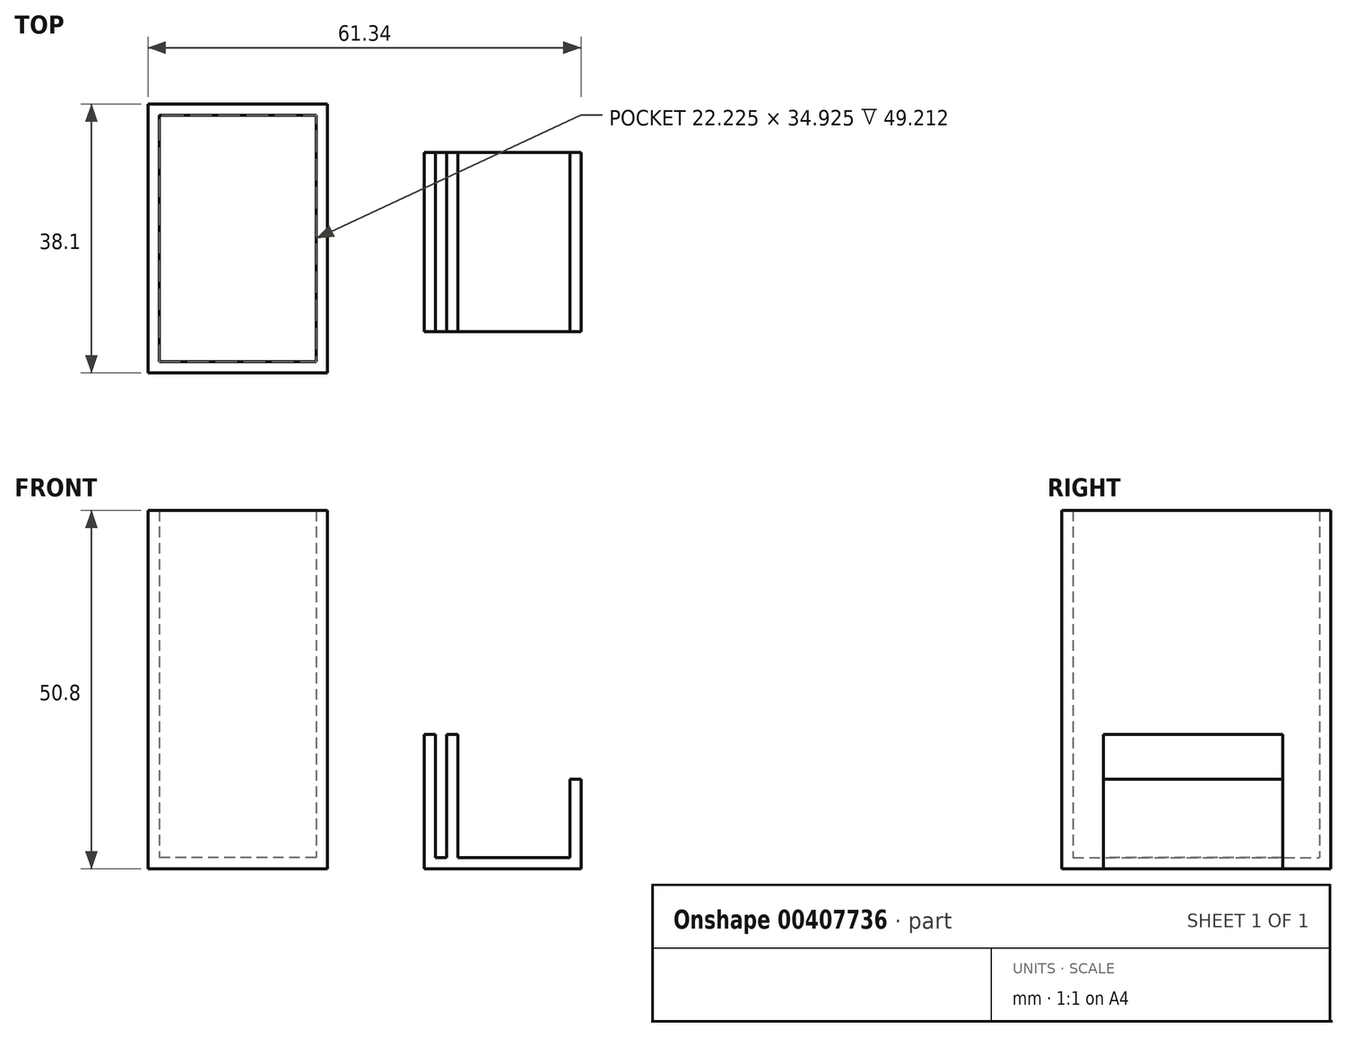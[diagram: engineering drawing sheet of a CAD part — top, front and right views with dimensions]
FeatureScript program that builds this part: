
annotation { "Feature Type Name" : "Feature", "Feature Type Description" : "" }
export const myFeature = defineFeature(function(context is Context, id is Id, definition is map)
    precondition{}
    {
        {
            var Q0;
            Q0=qCreatedBy(makeId("Top.planeOp"),FACE);
            var sketch = newSketch(context, id + "F0", { "sketchPlane" : qUnion([Q0])});
            skLineSegment(sketch, "E0.bottom", {"start": v(0, 0) * mm, "end": v(-25.4, 0) * mm});
            skLineSegment(sketch, "E0.top", {"start": v(0, 38.1) * mm, "end": v(-25.4, 38.1) * mm});
            skLineSegment(sketch, "E0.left", {"start": v(0, 0) * mm, "end": v(0, 38.1) * mm});
            skLineSegment(sketch, "E0.right", {"start": v(-25.4, 0) * mm, "end": v(-25.4, 38.1) * mm});
            skSolve(sketch);
        }
        {
            var Q0;
            Q0=makeQuery(id+"F0.imprint","IMPRINT",FACE,{"disambiguationData":[TD([[makeQuery(id+"F0.imprint","IMPRINT",EDGE,{"derivedFrom":sQuery(id+"F0.wireOp",EDGE,"E0.bottom")}),-1.0]])]});
            extrude(context, id + "F1", {"entities" : qUnion([Q0]), "depth" : 50.8 * mm});
        }
        {
            var Q0;
            Q0=makeQuery(id+"F1.opExtrude","CAP_FACE",FACE,{"disambiguationData":[OSD([sQuery(id+"F0.wireOp",EDGE,"E0.bottom"),sQuery(id+"F0.wireOp",EDGE,"E0.top"),sQuery(id+"F0.wireOp",EDGE,"E0.left"),sQuery(id+"F0.wireOp",EDGE,"E0.right")])],"isStart":false});
            shell(context, id + "F2", {"entities" : qUnion([Q0]), "thickness" : 1.59 * mm});
        }
        {
            var Q0;
            Q0=qCreatedBy(makeId("Top.planeOp"),FACE);
            var sketch = newSketch(context, id + "F3", { "sketchPlane" : qUnion([Q0])});
            skLineSegment(sketch, "E1.bottom", {"start": v(13.71, 5.85) * mm, "end": v(35.94, 5.85) * mm});
            skLineSegment(sketch, "E1.top", {"start": v(13.71, 31.25) * mm, "end": v(35.94, 31.25) * mm});
            skLineSegment(sketch, "E1.left", {"start": v(18.47, 5.85) * mm, "end": v(18.47, 31.25) * mm});
            skLineSegment(sketch, "E1.right", {"start": v(34.35, 5.85) * mm, "end": v(34.35, 31.25) * mm});
            skLineSegment(sketch, "E2.0", {"start": v(35.94, 5.85) * mm, "end": v(35.94, 31.25) * mm});
            skLineSegment(sketch, "E3.0", {"start": v(16.89, 5.85) * mm, "end": v(16.89, 31.25) * mm});
            skLineSegment(sketch, "E4.0", {"start": v(15.3, 5.85) * mm, "end": v(15.3, 31.25) * mm});
            skLineSegment(sketch, "E5.0", {"start": v(13.71, 5.85) * mm, "end": v(13.71, 31.25) * mm});
            skSolve(sketch);
        }
        {
            var Q0;
            {var subQ0=sQuery(id+"F3.wireOp",EDGE,"E1.left");Q0=makeQuery(id+"F3.imprint","IMPRINT",FACE,{"disambiguationData":[TD([[makeQuery(id+"F3.imprint","IMPRINT",EDGE,{"derivedFrom":subQ0}),-1.0]])]});}
            var Q1;
            {var subQ2=sQuery(id+"F3.wireOp",EDGE,"E1.right");Q1=makeQuery(id+"F3.imprint","IMPRINT",FACE,{"disambiguationData":[TD([[makeQuery(id+"F3.imprint","IMPRINT",EDGE,{"derivedFrom":subQ2}),-1.0]])]});}
            var Q2;
            {var subQ0=sQuery(id+"F3.wireOp",EDGE,"E1.left");Q2=makeQuery(id+"F3.imprint","IMPRINT",FACE,{"disambiguationData":[TD([[makeQuery(id+"F3.imprint","IMPRINT",EDGE,{"derivedFrom":subQ0}),1.0]])]});}
            var Q3;
            {var subQ0=sQuery(id+"F3.wireOp",EDGE,"E3.0");Q3=makeQuery(id+"F3.imprint","IMPRINT",FACE,{"disambiguationData":[TD([[makeQuery(id+"F3.imprint","IMPRINT",EDGE,{"derivedFrom":subQ0}),1.0]])]});}
            var Q4;
            {var subQ2=sQuery(id+"F3.wireOp",EDGE,"E4.0");Q4=makeQuery(id+"F3.imprint","IMPRINT",FACE,{"disambiguationData":[TD([[makeQuery(id+"F3.imprint","IMPRINT",EDGE,{"derivedFrom":subQ2}),1.0]])]});}
            extrude(context, id + "F4", {"entities" : qUnion([Q0, Q1, Q2, Q3, Q4]), "depth" : 1.59 * mm});
        }
        {
            var Q0;
            {var subQ2=sQuery(id+"F3.wireOp",EDGE,"E4.0");Q0=makeQuery(id+"F3.imprint","IMPRINT",FACE,{"disambiguationData":[TD([[makeQuery(id+"F3.imprint","IMPRINT",EDGE,{"derivedFrom":subQ2}),1.0]])]});}
            var Q1;
            {var subQ0=sQuery(id+"F3.wireOp",EDGE,"E1.left");Q1=makeQuery(id+"F3.imprint","IMPRINT",FACE,{"disambiguationData":[TD([[makeQuery(id+"F3.imprint","IMPRINT",EDGE,{"derivedFrom":subQ0}),1.0]])]});}
            extrude(context, id + "F5", {"entities" : qUnion([Q0, Q1]), "operationType" : NewBodyOperationType.ADD, "depth" : 19.05 * mm});
        }
        {
            var Q0;
            {var subQ2=sQuery(id+"F3.wireOp",EDGE,"E1.right");Q0=makeQuery(id+"F3.imprint","IMPRINT",FACE,{"disambiguationData":[TD([[makeQuery(id+"F3.imprint","IMPRINT",EDGE,{"derivedFrom":subQ2}),-1.0]])]});}
            extrude(context, id + "F6", {"entities" : qUnion([Q0]), "operationType" : NewBodyOperationType.ADD, "depth" : 12.7 * mm});
        }
    });
